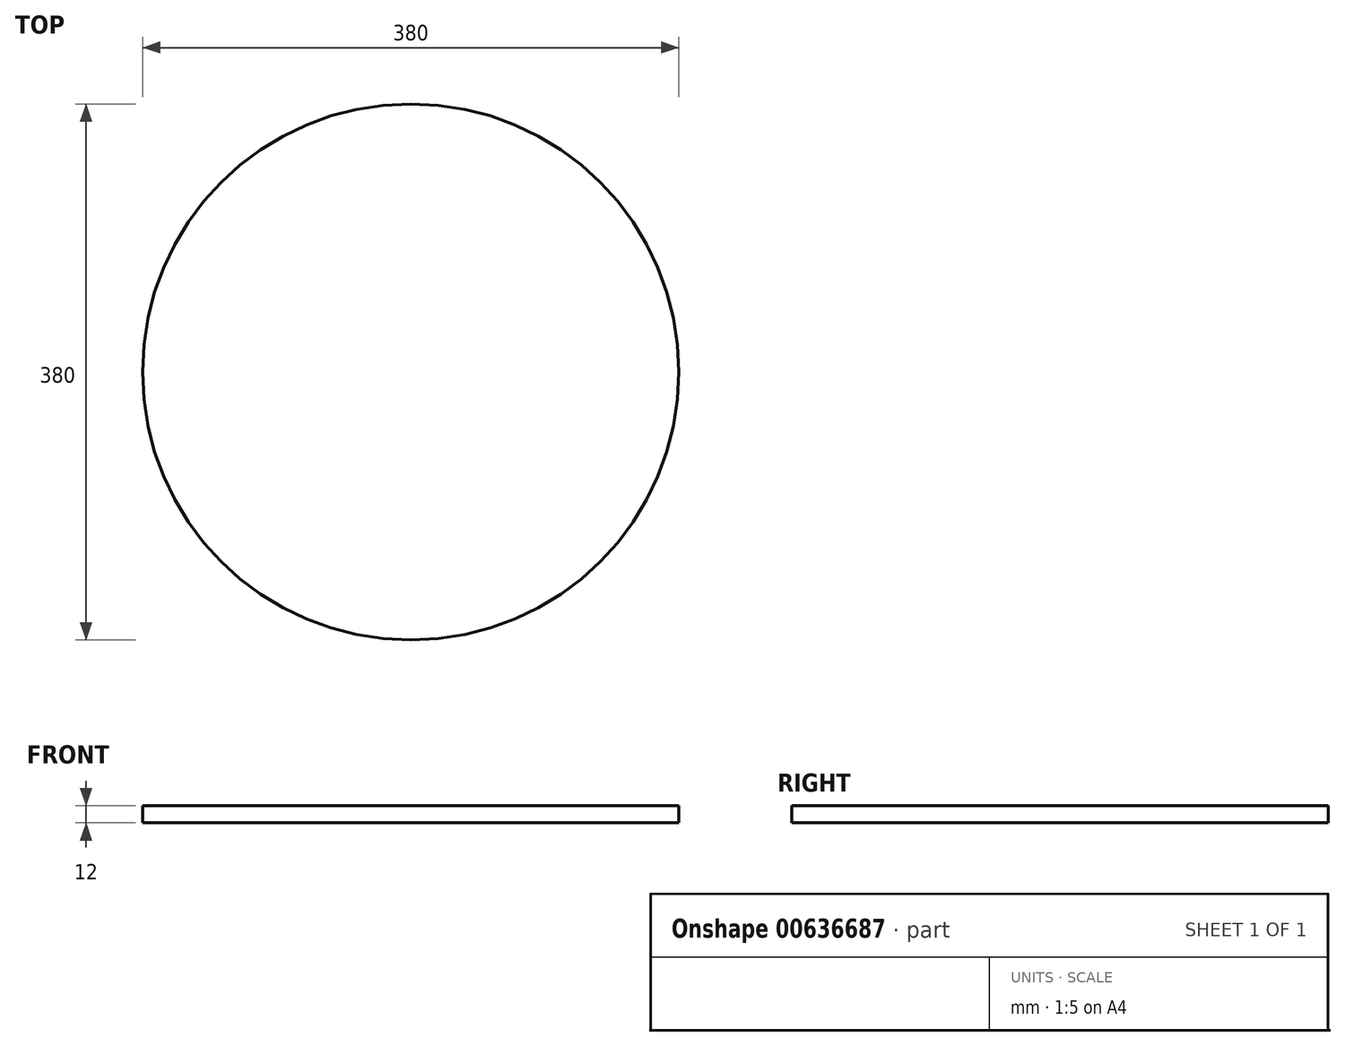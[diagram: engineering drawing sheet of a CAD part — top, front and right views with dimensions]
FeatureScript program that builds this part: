
annotation { "Feature Type Name" : "Feature", "Feature Type Description" : "" }
export const myFeature = defineFeature(function(context is Context, id is Id, definition is map)
    precondition{}
    {
        {
            var Q0;
            Q0=qCreatedBy(makeId("Top.planeOp"),FACE);
            var sketch = newSketch(context, id + "F0", { "sketchPlane" : qUnion([Q0])});
            skCircle(sketch, "E0", {"center": v(0, 0) * mm, "radius": 190 * mm});
            skSolve(sketch);
        }
        {
            var Q0;
            Q0 = qSketchRegion(id + "F0", true);
            extrude(context, id + "F1", {"entities" : qUnion([Q0]), "depth" : 12 * mm, "offsetDistance" : 25 * mm});
        }
    });
